# Revit family: pefy-p90_280mg9-f_50Hz
name_source: partatom
category: 機械設備
units: mm (PartAtom-declared; Revit-internal decimal feet)

## family parameters
OmniClass タイトル = Split System Air Conditioning Units
OmniClass 番号 = 23.75.10.24.21.27.27
パーツ タイプ = 標準
ロード時にボイドで切り取り = いいえ
丸型コネクタ寸法 = 直径を使用
作業面ベース = いいえ
共有 = いいえ
常に垂直 = はい
部屋計算ポイント = はい

## types (6) — shared parameters
Clearance Back = 50  [stored 0.164042 ft]
Clearance Bottom = 20  [stored 0.0656168 ft]
Clearance Right = 50  [stored 0.164042 ft]
Clearance Top = 20  [stored 0.0656168 ft]
IfcExportAs = IfcUnitaryEquipmentType
IfcExportType = AIRCONDITIONINGUNIT
OmniClassCode = 23-33 17 13 11
URL = https://www.mitsubishielectric.co.jp
Uniclass2015Code = Pr_70_65_03_84
Uniclass2015Title = Split coil remote air cooled condensing units
Uniclass2015Version = Systems v1.9
ケーブルサイズ = 2 mm
サービススペース = はい
ドレン管径 = 32 mm
仕様書バージョン = Version1.0
企業コード = 108420
冷媒液管径 = 10 mm
冷媒管径 = 100 mm
冷媒高低圧ガス管径 = 0 mm
分類コード = 50053003221070
加湿給水管径 = 0 mm
参照している仕様書等のバージョン = 公共建築工事標準仕様書（機械設備工事編）平成31年度版
吊りボルト_H = 41  [stored 0.134514 ft]
周波数 = 50 Hz
呼称 = 室内機_天井吊(隠ぺい)形(両ダクト形)
形式 = 天井吊（隠ぺい）形（両ダクト形）
推奨ブレーカー容量 = 0 A
本体マテリアル = <カテゴリ別>
極数 = 3
法定耐用年数 = 15
消費電力_加湿器 = 0.00 kW
消費電力_電気ヒーター = 0.00 kW
点検口 = はい
点検口位置 = 200  [stored 0.656168 ft]
相_電気ヒーター = 1
積算_科目 = 1 空気調和設備
符号 = ACP_CID
製品リリース年月 = 2022年9月15日
製品出荷対象 = 国内
製造元 = 三菱電機株式会社
設置方法 = 天井吊(隠ぺい)形
設計冷房能力 = 0 kW
設計冷房能力_顕熱 = 0 kW
設計暖房能力 = 0.00 kW
説明 = ビル用マルチエアコン オールフレッシュ　室内機
負荷分類 = 3_ファン類
運転質量 = 0.00 kg
電圧 = 200 V
電圧_電気ヒーター = 0 V
zero-valued in all types: 有効加湿量, 電源_H

## per-type parameters (varying)
- PEFY-P90MG9-F: Clearance Front=575  [stored 1.88648 ft]; Clearance Left=980  [stored 3.21522 ft]; Depth=900  [stored 2.95276 ft]; Height=380  [stored 1.24672 ft]; MAX風量=540.0 m³/h; RAサイズ_D=340  [stored 1.11549 ft]; RAサイズ_W=850  [stored 2.78871 ft]; SAサイズ_D=250  [stored 0.82021 ft]; SAサイズ_W=800  [stored 2.62467 ft]; S_H=400  [stored 1.31234 ft]; Width=1000  [stored 3.28084 ft]; ドレン管_横=387  [stored 1.26969 ft]; ドレン管_縦=328  [stored 1.07612 ft]; 冷媒ガス管_横=200  [stored 0.656168 ft]; 冷媒ガス管_縦=130  [stored 0.426509 ft]; 冷媒ガス管径=16 mm; 冷媒液管_横=92  [stored 0.301837 ft]; 冷媒液管_縦=77  [stored 0.252625 ft]; 冷媒管径符号=Bd; 冷房能力=9 kW; 吊り位置X=1004  [stored 3.29396 ft]; 吊り位置Y=814  [stored 2.6706 ft]; 吊り幅=60  [stored 0.19685 ft]; 暖房能力=8.50 kW; 機外静圧=130.0 Pa; 消費電力=0.13 kW; 消費電力_冷房=0.13 kW; 消費電力_暖房=0.13 kW; 点検口設置範囲=700  [stored 2.29659 ft]; 相=1; 製品質量=52.00 kg; 質量=62.40 kg; 電動機出力_送風機=0.07 kW; 音響パワーレベル(dB)=58; 風量=540.0 m³/h; 風量（m3／min）=9
- PEFY-P112MG9-F: Clearance Front=575  [stored 1.88648 ft]; Clearance Left=1180  [stored 3.87139 ft]; Depth=900  [stored 2.95276 ft]; Height=380  [stored 1.24672 ft]; MAX風量=840.0 m³/h; RAサイズ_D=340  [stored 1.11549 ft]; RAサイズ_W=1050; SAサイズ_D=250  [stored 0.82021 ft]; SAサイズ_W=1000  [stored 3.28084 ft]; S_H=400  [stored 1.31234 ft]; Width=1200; ドレン管_横=387  [stored 1.26969 ft]; ドレン管_縦=328  [stored 1.07612 ft]; 冷媒ガス管_横=200  [stored 0.656168 ft]; 冷媒ガス管_縦=130  [stored 0.426509 ft]; 冷媒ガス管径=16 mm; 冷媒液管_横=92  [stored 0.301837 ft]; 冷媒液管_縦=77  [stored 0.252625 ft]; 冷媒管径符号=Bd; 冷房能力=11.2 kW; 吊り位置X=1204; 吊り位置Y=814  [stored 2.6706 ft]; 吊り幅=60  [stored 0.19685 ft]; 暖房能力=10.60 kW; 機外静圧=130.0 Pa; 消費電力=0.20 kW; 消費電力_冷房=0.20 kW; 消費電力_暖房=0.20 kW; 点検口設置範囲=700  [stored 2.29659 ft]; 相=1; 製品質量=68.00 kg; 質量=81.60 kg; 電動機出力_送風機=0.08 kW; 音響パワーレベル(dB)=60; 風量=840.0 m³/h; 風量（m3／min）=14
- PEFY-P140MG9-F: Clearance Front=575  [stored 1.88648 ft]; Clearance Left=1180  [stored 3.87139 ft]; Depth=900  [stored 2.95276 ft]; Height=380  [stored 1.24672 ft]; MAX風量=840.0 m³/h; RAサイズ_D=340  [stored 1.11549 ft]; RAサイズ_W=1050; SAサイズ_D=250  [stored 0.82021 ft]; SAサイズ_W=1000  [stored 3.28084 ft]; S_H=400  [stored 1.31234 ft]; Width=1200; ドレン管_横=387  [stored 1.26969 ft]; ドレン管_縦=328  [stored 1.07612 ft]; 冷媒ガス管_横=200  [stored 0.656168 ft]; 冷媒ガス管_縦=130  [stored 0.426509 ft]; 冷媒ガス管径=16 mm; 冷媒液管_横=92  [stored 0.301837 ft]; 冷媒液管_縦=77  [stored 0.252625 ft]; 冷媒管径符号=Bd; 冷房能力=14 kW; 吊り位置X=1204; 吊り位置Y=814  [stored 2.6706 ft]; 吊り幅=60  [stored 0.19685 ft]; 暖房能力=13.20 kW; 機外静圧=130.0 Pa; 消費電力=0.21 kW; 消費電力_冷房=0.20 kW; 消費電力_暖房=0.21 kW; 点検口設置範囲=700  [stored 2.29659 ft]; 相=1; 製品質量=68.00 kg; 質量=81.60 kg; 電動機出力_送風機=0.08 kW; 音響パワーレベル(dB)=61; 風量=840.0 m³/h; 風量（m3／min）=14
- PEFY-P160MG9-F: Clearance Front=575  [stored 1.88648 ft]; Clearance Left=1180  [stored 3.87139 ft]; Depth=900  [stored 2.95276 ft]; Height=380  [stored 1.24672 ft]; MAX風量=1080.0 m³/h; RAサイズ_D=340  [stored 1.11549 ft]; RAサイズ_W=1050; SAサイズ_D=250  [stored 0.82021 ft]; SAサイズ_W=1000  [stored 3.28084 ft]; S_H=400  [stored 1.31234 ft]; Width=1200; ドレン管_横=387  [stored 1.26969 ft]; ドレン管_縦=328  [stored 1.07612 ft]; 冷媒ガス管_横=200  [stored 0.656168 ft]; 冷媒ガス管_縦=130  [stored 0.426509 ft]; 冷媒ガス管径=16 mm; 冷媒液管_横=92  [stored 0.301837 ft]; 冷媒液管_縦=77  [stored 0.252625 ft]; 冷媒管径符号=Bd; 冷房能力=16 kW; 吊り位置X=1204; 吊り位置Y=814  [stored 2.6706 ft]; 吊り幅=60  [stored 0.19685 ft]; 暖房能力=15.10 kW; 機外静圧=130.0 Pa; 消費電力=0.20 kW; 消費電力_冷房=0.20 kW; 消費電力_暖房=0.20 kW; 点検口設置範囲=700  [stored 2.29659 ft]; 相=1; 製品質量=68.00 kg; 質量=81.60 kg; 電動機出力_送風機=0.09 kW; 音響パワーレベル(dB)=62; 風量=1080.0 m³/h; 風量（m3／min）=18
- PEFY-P224MG9-F: Clearance Front=680  [stored 2.23097 ft]; Clearance Left=1300; Depth=1120  [stored 3.67454 ft]; Height=470  [stored 1.54199 ft]; MAX風量=1680.0 m³/h; RAサイズ_D=420  [stored 1.37795 ft]; RAサイズ_W=1100  [stored 3.60892 ft]; SAサイズ_D=340  [stored 1.11549 ft]; SAサイズ_W=1100  [stored 3.60892 ft]; S_H=490  [stored 1.60761 ft]; Width=1250; ドレン管_横=489  [stored 1.60433 ft]; ドレン管_縦=327; 冷媒ガス管_横=249  [stored 0.816929 ft]; 冷媒ガス管_縦=164  [stored 0.538058 ft]; 冷媒ガス管径=19 mm; 冷媒液管_横=95; 冷媒液管_縦=44  [stored 0.144357 ft]; 冷媒管径符号=Be; 冷房能力=22.4 kW; 吊り位置X=1326; 吊り位置Y=1034  [stored 3.39239 ft]; 吊り幅=61  [stored 0.200131 ft]; 暖房能力=21.20 kW; 機外静圧=200.0 Pa; 消費電力=0.32 kW; 消費電力_冷房=0.32 kW; 消費電力_暖房=0.32 kW; 点検口設置範囲=800  [stored 2.62467 ft]; 相=3; 製品質量=92.00 kg; 質量=110.40 kg; 電動機出力_送風機=0.20 kW; 音響パワーレベル(dB)=67; 風量=1680.0 m³/h; 風量（m3／min）=28
- PEFY-P280MG9-F: Clearance Front=680  [stored 2.23097 ft]; Clearance Left=1300; Depth=1120  [stored 3.67454 ft]; Height=470  [stored 1.54199 ft]; MAX風量=2100.0 m³/h; RAサイズ_D=420  [stored 1.37795 ft]; RAサイズ_W=1100  [stored 3.60892 ft]; SAサイズ_D=340  [stored 1.11549 ft]; SAサイズ_W=1100  [stored 3.60892 ft]; S_H=490  [stored 1.60761 ft]; Width=1250; ドレン管_横=489  [stored 1.60433 ft]; ドレン管_縦=327; 冷媒ガス管_横=249  [stored 0.816929 ft]; 冷媒ガス管_縦=164  [stored 0.538058 ft]; 冷媒ガス管径=22 mm; 冷媒液管_横=95; 冷媒液管_縦=44  [stored 0.144357 ft]; 冷媒管径符号=Bf; 冷房能力=28 kW; 吊り位置X=1326; 吊り位置Y=1034  [stored 3.39239 ft]; 吊り幅=61  [stored 0.200131 ft]; 暖房能力=26.50 kW; 機外静圧=200.0 Pa; 消費電力=0.34 kW; 消費電力_冷房=0.34 kW; 消費電力_暖房=0.34 kW; 点検口設置範囲=800  [stored 2.62467 ft]; 相=3; 製品質量=97.00 kg; 質量=116.40 kg; 電動機出力_送風機=0.23 kW; 音響パワーレベル(dB)=71; 風量=2100.0 m³/h; 風量（m3／min）=35

note: column(s) folded — value = type name in every type: モデル

note: [stored X ft] marks values corroborated as IEEE doubles in the binary element streams (Revit-internal decimal feet)

## geometry (parser evidence)
native form markers: Blend x4
no freeform markers — native parametric forms only
